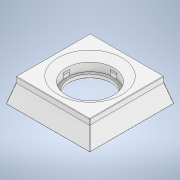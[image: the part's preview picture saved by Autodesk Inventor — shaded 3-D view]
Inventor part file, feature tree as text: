
AUTODESK INVENTOR PART (.ipt)
format: ipt  version: 2020.5 (Build 245400000, 400)  size: 281,600 bytes
history: native  units: in
note: dims shown in document units (in); Inventor stores cm internally (conversion verified against a paired STEP export)
features: sketch x10, sweep x8, extrude x6, chamfer x2, plane x1
ambient origin geometry x8: Origin, YZ Plane, XZ Plane, XY Plane, X Axis, Y Axis, Z Axis, Center Point
bodies: Solid1 (feature_tree)
feature tree (27):
  plane  "Work Plane1"
  sketch  "Sketch1"  dims[d44=0.2362in d45=0.0in d46=0.0787in d47=0.0in]
  extrude  "Extrusion1"  Depth=0.0787in TaperAngle=0.0deg
  extrude  "Extrusion2"  Depth=0.3937in
  sweep  "Sweep7"
  sweep  "Sweep8"
  sweep  "Sweep9"
  sweep  "Sweep10"
  sweep  "Sweep11"
  sweep  "Sweep12"
  sweep  "Sweep13"
  sweep  "Sweep14"
  extrude  "Extrusion4"  Depth=0.1181in TaperAngle=0.0deg
  extrude  "Extrusion5"  Depth=0.3937in TaperAngle=0.0deg
  chamfer  "Chamfer1"  Distance=0.0787in Angle=45.0deg
  extrude  "Extrusion6"  Depth=0.3937in TaperAngle=0.0deg
  extrude  "Extrusion7"  Depth=0.3937in
  chamfer  "Chamfer4"  Distance=0.3937in
  sketch  "3D Sketch7"
  sketch  "3D Sketch8"
  sketch  "3D Sketch9"
  sketch  "3D Sketch10"
  sketch  "3D Sketch11"
  sketch  "3D Sketch12"
  sketch  "3D Sketch13"
  sketch  "3D Sketch14"
  sketch  "Sketch2"  dims[d48=4.3307in d50=4.3307in d57=0.0in d58=0.0in d59=0.0in d60=0.0in d61=0.0in d62=0.0in d63=0.0in d64=0.0in d65=0.0in d66=0.0in d67=0.0in d68=0.0in d69=0.0in d70=0.0in d71=0.0in d72=0.0in d73=0.1181in d74=0.0in d75=1.9685in d76=0.0in d80=0.0098in d81=0.0787in d82=45.0deg d95=0.0394in d96=0.0in d100=1.0118in d101=0.3937in d102=0.0in d103=0.1772in d104=0.0984in d105=45.0deg]
